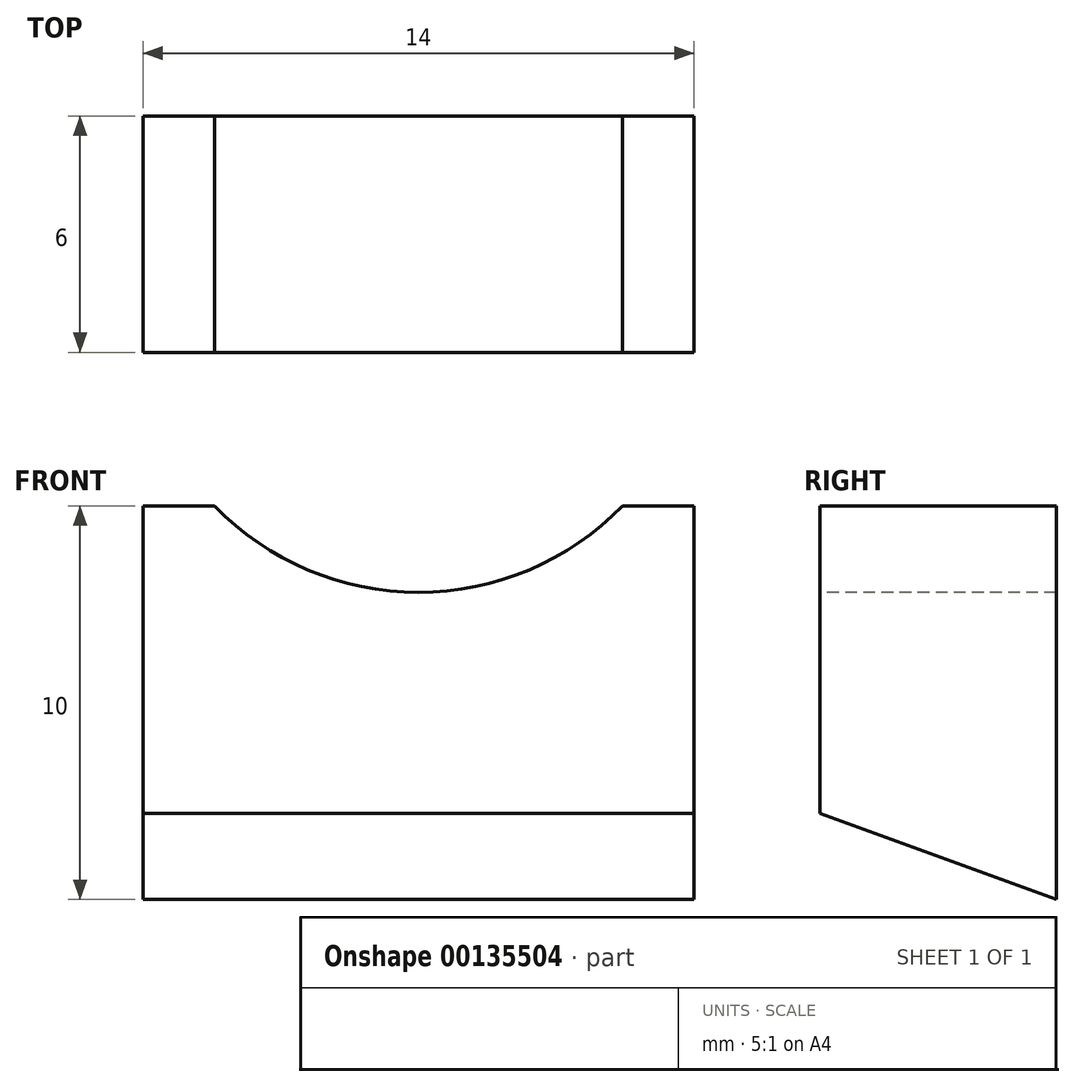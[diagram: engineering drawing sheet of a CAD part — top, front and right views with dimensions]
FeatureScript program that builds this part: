
annotation { "Feature Type Name" : "Feature", "Feature Type Description" : "" }
export const myFeature = defineFeature(function(context is Context, id is Id, definition is map)
    precondition{}
    {
        {
            var Q0;
            Q0=qCreatedBy(makeId("Top.planeOp"),FACE);
            var sketch = newSketch(context, id + "F0", { "sketchPlane" : qUnion([Q0])});
            skLineSegment(sketch, "E0.bottom", {"start": v(7, 3) * mm, "end": v(-7, 3) * mm});
            skLineSegment(sketch, "E0.top", {"start": v(7, -3) * mm, "end": v(-7, -3) * mm});
            skLineSegment(sketch, "E0.left", {"start": v(7, 3) * mm, "end": v(7, -3) * mm});
            skLineSegment(sketch, "E0.right", {"start": v(-7, 3) * mm, "end": v(-7, -3) * mm});
            skPoint(sketch, "E0.middle", {"position": v(0, 0) * mm});
            skSolve(sketch);
        }
        {
            var Q0;
            Q0=makeQuery(id+"F0.imprint","IMPRINT",FACE,{"disambiguationData":[TD([[makeQuery(id+"F0.imprint","IMPRINT",EDGE,{"derivedFrom":sQuery(id+"F0.wireOp",EDGE,"E0.bottom")}),1.0]])]});
            extrude(context, id + "F1", {"entities" : qUnion([Q0]), "depth" : 10 * mm});
        }
        {
            var Q0;
            Q0=makeQuery(id+"F1.opExtrude","SWEPT_FACE",FACE,{"disambiguationData":[OSD([sQuery(id+"F0.wireOp",EDGE,"E0.top")])]});
            var sketch = newSketch(context, id + "F2", { "sketchPlane" : qUnion([Q0])});
            skCircle(sketch, "E1", {"center": v(0, 15) * mm, "radius": 7.2 * mm});
            skSolve(sketch);
        }
        {
            var Q0;
            {var subQ0=sQuery(id+"F2.wireOp",EDGE,"E1");var subQ1=makeQuery(id+"F1.opExtrude","CAP_EDGE",EDGE,{"disambiguationData":[OSD([sQuery(id+"F0.wireOp",EDGE,"E0.top")])],"isStart":false});var subQ2=makeQuery(id+"F2.imprint","INTERSECT",VERTEX,{"disambiguationData":[OD(0.0)],"derivedFrom":[subQ1,subQ0]});Q0=makeQuery(id+"F2.imprint","IMPRINT",FACE,{"disambiguationData":[TD([[makeQuery(id+"F2.imprint","IMPRINT",EDGE,{"disambiguationData":[TD([[subQ2,1.0]])],"derivedFrom":subQ0}),1.0]])]});}
            var Q1;
            {var subQ0=sQuery(id+"F2.wireOp",EDGE,"E1");var subQ1=makeQuery(id+"F1.opExtrude","CAP_EDGE",EDGE,{"disambiguationData":[OSD([sQuery(id+"F0.wireOp",EDGE,"E0.top")])],"isStart":false});var subQ2=makeQuery(id+"F2.imprint","INTERSECT",VERTEX,{"disambiguationData":[OD(0.0)],"derivedFrom":[subQ1,subQ0]});Q1=makeQuery(id+"F2.imprint","IMPRINT",FACE,{"disambiguationData":[TD([[makeQuery(id+"F2.imprint","IMPRINT",EDGE,{"disambiguationData":[TD([[subQ2,-1.0]])],"derivedFrom":subQ0}),1.0]])]});}
            extrude(context, id + "F3", {"entities" : qUnion([Q0, Q1]), "operationType" : NewBodyOperationType.REMOVE, "oppositeDirection" : true, "depth" : 25 * mm});
        }
        {
            var Q0;
            Q0=makeQuery(id+"F1.opExtrude","SWEPT_FACE",FACE,{"disambiguationData":[OSD([sQuery(id+"F0.wireOp",EDGE,"E0.right")])]});
            var sketch = newSketch(context, id + "F4", { "sketchPlane" : qUnion([Q0])});
            skLineSegment(sketch, "E2", {"start": v(-3, 0) * mm, "end": v(3, 2.18) * mm});
            skSolve(sketch);
        }
        {
            var Q0;
            Q0 = qSketchRegion(id + "F4", true);
            var Q1;
            {var subQ0=sQuery(id+"F4.wireOp",EDGE,"E2");Q1=makeQuery(id+"F4.imprint","IMPRINT",FACE,{"disambiguationData":[TD([[makeQuery(id+"F4.imprint","IMPRINT",EDGE,{"derivedFrom":subQ0}),-1.0]])]});}
            extrude(context, id + "F5", {"entities" : qUnion([Q0, Q1]), "operationType" : NewBodyOperationType.REMOVE, "oppositeDirection" : true, "depth" : 25 * mm});
        }
    });
